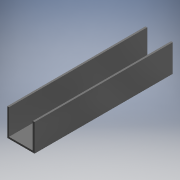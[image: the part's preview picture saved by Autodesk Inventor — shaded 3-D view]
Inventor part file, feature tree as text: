
AUTODESK INVENTOR PART (.ipt)
format: ipt  version: 2019 (Build 230136000, 136)  size: 108,544 bytes
history: native  units: mm (DEFAULTED — no unit token found)
features: extrude x3, sketch x3
ambient origin geometry x8: Origin, YZ Plane, XZ Plane, XY Plane, X Axis, Y Axis, Z Axis, Center Point
bodies: Solid1 (feature_tree)
feature tree (6):
  extrude  "Extrusion1"  Depth=31.75mm
  extrude  "Extrusion2"  Depth=160.3375mm
  extrude  "Extrusion3"  Depth=29.718mm
  sketch  "Sketch1"  dims[d0=31.75mm d1=31.75mm]
  sketch  "Sketch2"  dims[d2=160.3375mm d3=0.0mm d4=5.08mm]
  sketch  "Sketch3"  dims[d5=31.75mm d6=15.875mm d7=15.875mm d8=269.24mm d9=0.0mm d10=0.0mm d11=2.032mm d12=2.032mm d13=0.0mm d14=29.718mm d15=0.0mm]
